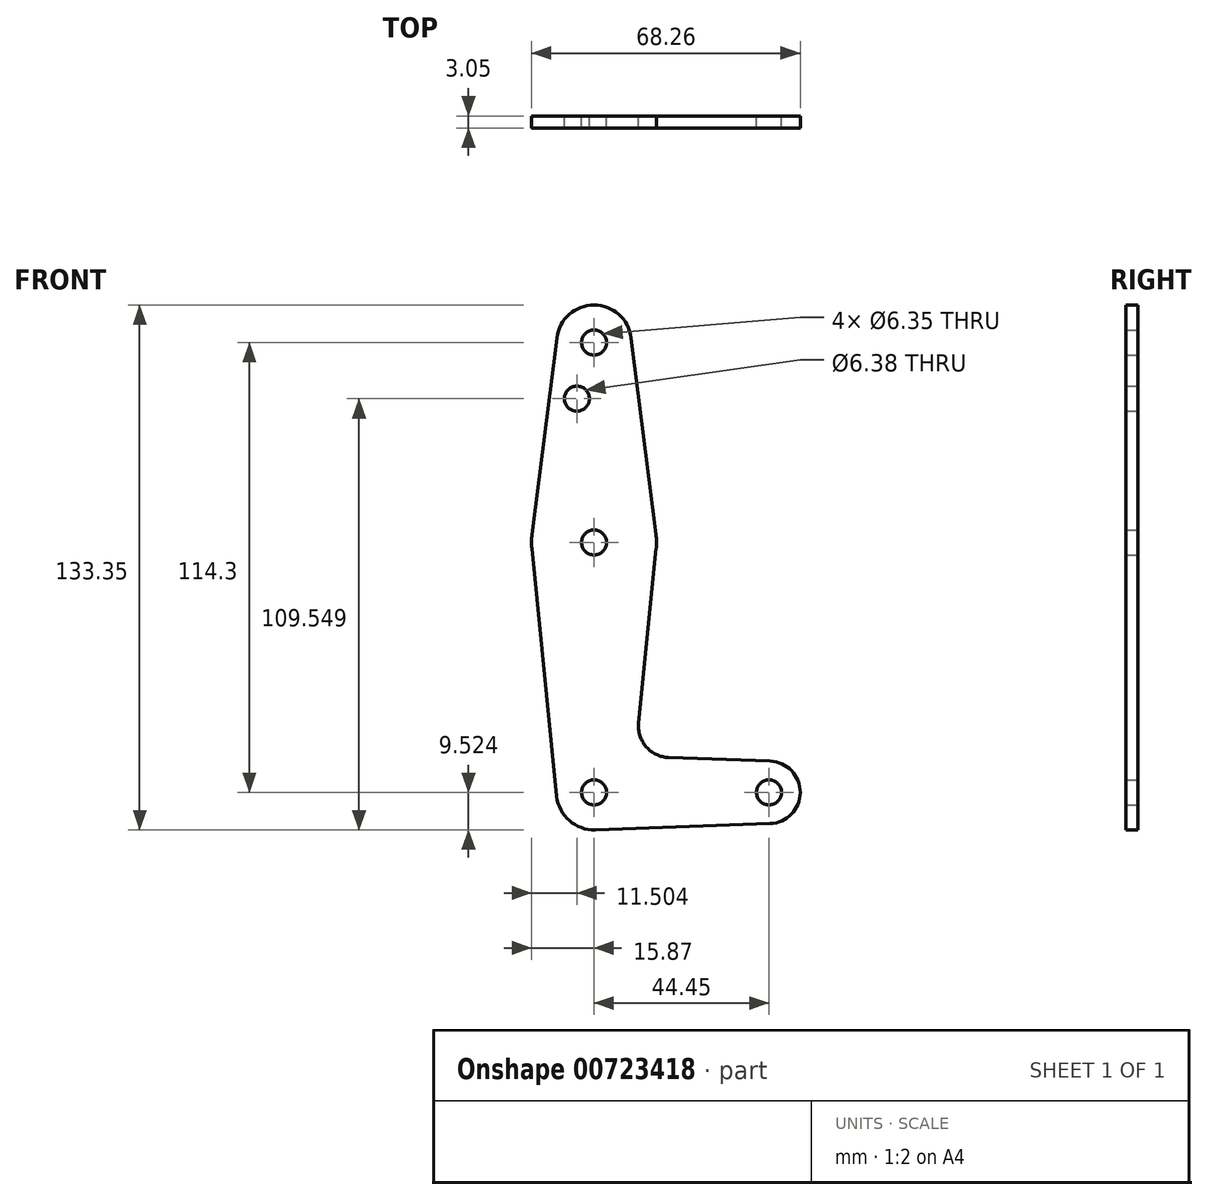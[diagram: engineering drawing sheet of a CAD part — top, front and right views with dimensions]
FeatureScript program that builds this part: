
annotation { "Feature Type Name" : "Feature", "Feature Type Description" : "" }
export const myFeature = defineFeature(function(context is Context, id is Id, definition is map)
    precondition{}
    {
        {
            var Q0;
            Q0=qCreatedBy(makeId("Front.planeOp"),FACE);
            var sketch = newSketch(context, id + "F0", { "sketchPlane" : qUnion([Q0])});
            skLineSegment(sketch, "E0", {"start": v(0, 73.33) * mm, "end": v(0, -40.97) * mm});
            skLineSegment(sketch, "E1", {"start": v(0, -40.97) * mm, "end": v(44.45, -40.97) * mm, "construction": true});
            skCircle(sketch, "E2", {"center": v(0, 73.33) * mm, "radius": 9.53 * mm});
            skCircle(sketch, "E3", {"center": v(0, 22.53) * mm, "radius": 15.88 * mm});
            skLineSegment(sketch, "E4", {"start": v(9.45, 74.52) * mm, "end": v(15.75, 24.52) * mm});
            skLineSegment(sketch, "E5", {"start": v(0, -40.97) * mm, "end": v(0, 73.33) * mm, "construction": true});
            skCircle(sketch, "E6", {"center": v(0, -40.97) * mm, "radius": 9.53 * mm});
            skCircle(sketch, "E7", {"center": v(44.45, -40.97) * mm, "radius": 7.94 * mm});
            skLineSegment(sketch, "E8", {"start": v(-9.45, 74.52) * mm, "end": v(-15.75, 24.52) * mm});
            skLineSegment(sketch, "E9", {"start": v(-15.8, 20.95) * mm, "end": v(-9.48, -41.92) * mm});
            skLineSegment(sketch, "E10", {"start": v(15.8, 20.95) * mm, "end": v(11.34, -23.37) * mm});
            skLineSegment(sketch, "E11", {"start": v(44.73, -33.03) * mm, "end": v(18.97, -32.11) * mm});
            skLineSegment(sketch, "E12", {"start": v(0.34, -50.49) * mm, "end": v(44.73, -48.9) * mm});
            skArc(sketch, "E13.filletArc", {"start": v(11.34, -23.37) * mm, "mid": v(13.26, -29.4) * mm, "end": v(18.97, -32.11) * mm});
            skCircle(sketch, "E14", {"center": v(0, 22.53) * mm, "radius": 3.18 * mm});
            skCircle(sketch, "E15", {"center": v(0, -40.97) * mm, "radius": 3.18 * mm});
            skCircle(sketch, "E16", {"center": v(0, 73.33) * mm, "radius": 3.18 * mm});
            skCircle(sketch, "E17", {"center": v(44.45, -40.97) * mm, "radius": 3.18 * mm});
            skCircle(sketch, "E18", {"center": v(-4.37, 59.06) * mm, "radius": 3.19 * mm});
            skSolve(sketch);
        }
        {
            var Q0;
            Q0 = qSketchRegion(id + "F0", true);
            extrude(context, id + "F1", {"entities" : qUnion([Q0]), "depth" : 3.05 * mm, "offsetDistance" : 25.4 * mm});
        }
    });
